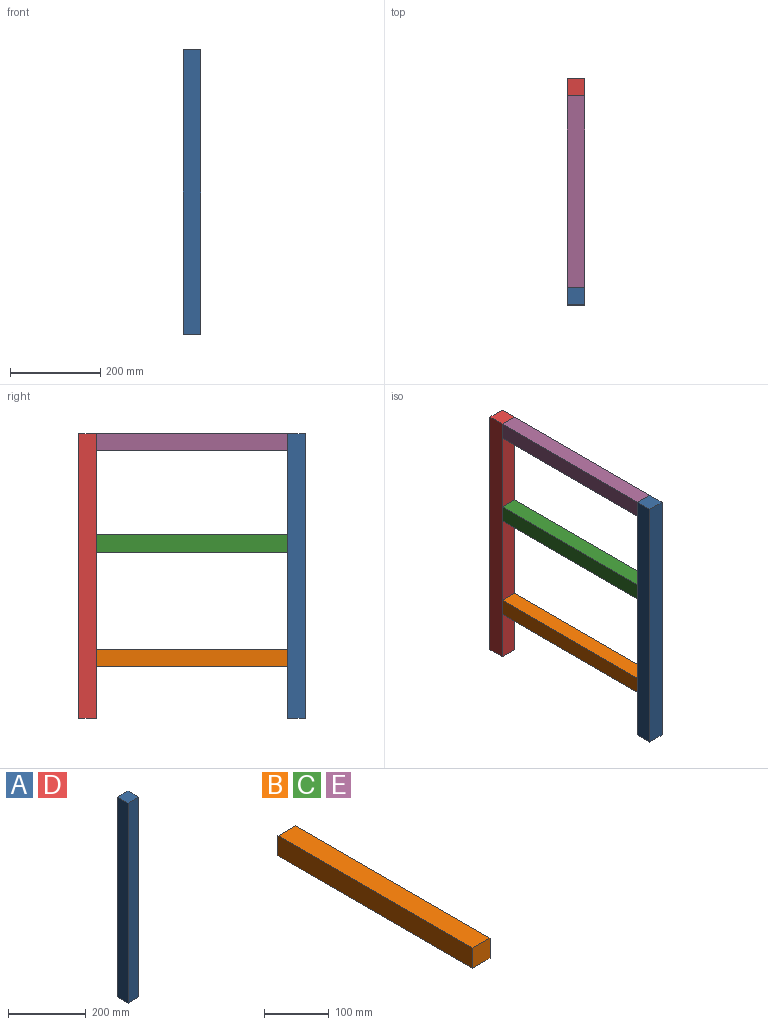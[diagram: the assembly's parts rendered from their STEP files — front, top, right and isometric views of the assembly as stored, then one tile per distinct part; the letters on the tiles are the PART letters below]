
ASSEMBLY  parts=5 mates=4
PART A: 6 faces, bbox 38x38x630 mm
  f0: plane 38x38mm, normal (0,0,1), area 1444mm2, adj f1,f3,f4,f5
  f1: plane 630x38mm, normal (-1,0,0), area 23940mm2, adj f0,f2,f4,f5
  f2: plane 38x38mm, normal (0,0,-1), area 1444mm2, adj f1,f3,f4,f5
  f3: plane 630x38mm, normal (1,0,0), area 23940mm2, adj f0,f2,f4,f5
  f4: plane 630x38mm, normal (0,-1,0), area 23940mm2, adj f0,f1,f2,f3
  f5: plane 630x38mm, normal (0,1,0), area 23940mm2, adj f0,f1,f2,f3
PART B: 6 faces, bbox 38x424x38 mm
  f0: plane 424x38mm, normal (0,0,1), area 16112mm2, adj f1,f3,f4,f5
  f1: plane 38x38mm, normal (0,-1,0), area 1444mm2, adj f0,f2,f4,f5
  f2: plane 424x38mm, normal (0,0,-1), area 16112mm2, adj f1,f3,f4,f5
  f3: plane 38x38mm, normal (0,1,0), area 1444mm2, adj f0,f2,f4,f5
  f4: plane 424x38mm, normal (1,0,0), area 16112mm2, adj f0,f1,f2,f3
  f5: plane 424x38mm, normal (-1,0,0), area 16112mm2, adj f0,f1,f2,f3
PART C: same geometry as B
PART D: same geometry as A
PART E: same geometry as B
PLACE A t=(-47.42,-189.63,140.68)mm
PLACE B t=(-85.42,234.37,255.68)mm
PLACE C t=(-85.42,234.37,508.68)mm
PLACE D t=(-47.42,272.37,140.68)mm
PLACE E t=(-85.42,234.37,732.68)mm
MATE fastened B.f1 <-> A.f5  axis (0,-1,0) through (-66.42,-189.63,255.68)mm
MATE fastened D.f4 <-> E.f3  axis (0,-1,0) through (-66.42,234.37,770.68)mm
MATE fastened C.f1 <-> A.f5  axis (0,-1,0) through (-66.42,-189.63,508.68)mm
MATE fastened A.f5 <-> E.f1  axis (0,1,0) through (-66.42,-189.63,770.68)mm
